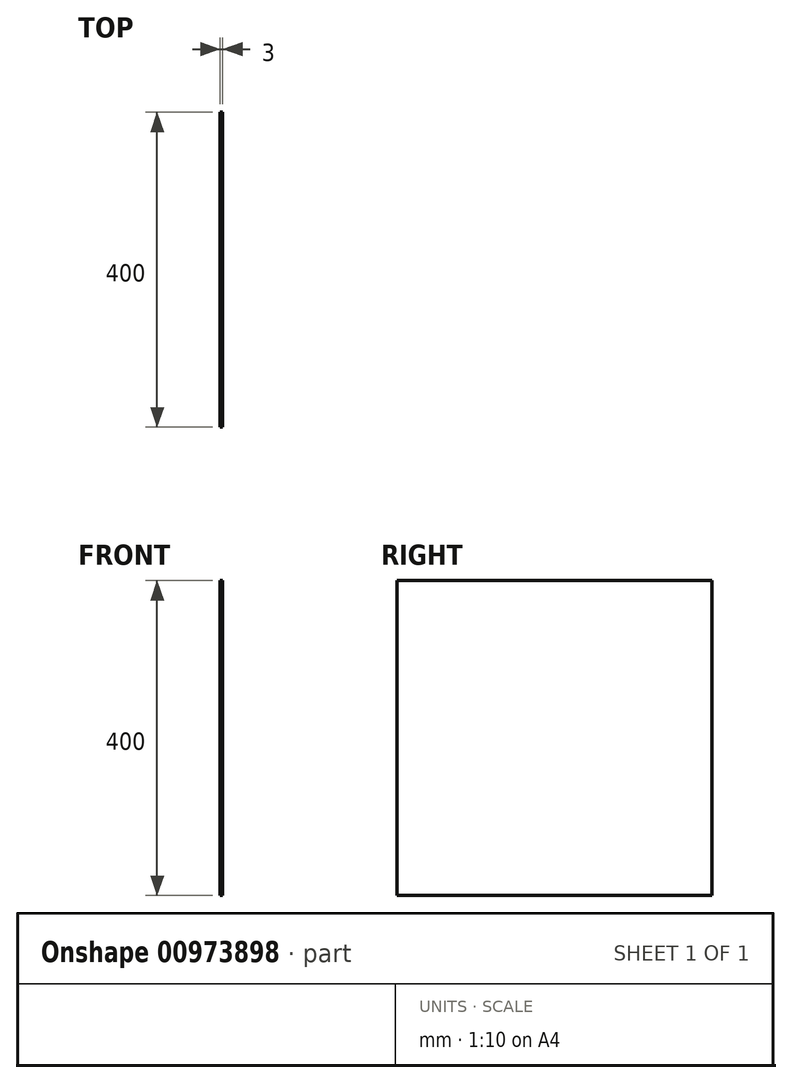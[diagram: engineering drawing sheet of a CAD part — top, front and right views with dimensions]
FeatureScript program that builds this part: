
annotation { "Feature Type Name" : "Feature", "Feature Type Description" : "" }
export const myFeature = defineFeature(function(context is Context, id is Id, definition is map)
    precondition{}
    {
        {
            var Q0;
            Q0=qCreatedBy(makeId("Right.planeOp"),FACE);
            var sketch = newSketch(context, id + "F0", { "sketchPlane" : qUnion([Q0])});
            skLineSegment(sketch, "E0.bottom", {"start": v(-200, 200) * mm, "end": v(200, 200) * mm});
            skLineSegment(sketch, "E0.top", {"start": v(-200, -200) * mm, "end": v(200, -200) * mm});
            skLineSegment(sketch, "E0.left", {"start": v(-200, 200) * mm, "end": v(-200, -200) * mm});
            skLineSegment(sketch, "E0.right", {"start": v(200, 200) * mm, "end": v(200, -200) * mm});
            skPoint(sketch, "E0.middle", {"position": v(0, 0) * mm});
            skSolve(sketch);
        }
        {
            var Q0;
            Q0=makeQuery(id+"F0.imprint","IMPRINT",FACE,{"disambiguationData":[TD([[makeQuery(id+"F0.imprint","IMPRINT",EDGE,{"derivedFrom":sQuery(id+"F0.wireOp",EDGE,"E0.bottom")}),-1.0]])]});
            extrude(context, id + "F1", {"entities" : qUnion([Q0]), "depth" : 3 * mm, "offsetDistance" : 25 * mm});
        }
    });
